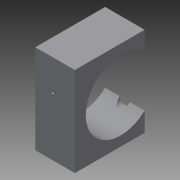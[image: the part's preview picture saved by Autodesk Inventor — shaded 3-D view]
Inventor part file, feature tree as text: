
AUTODESK INVENTOR PART (.ipt)
format: ipt  version: 2015 SP2 (Build 190223200, 223)  size: 101,888 bytes
history: native  units: mm
features: sketch x6, hole x3, extrude x1
ambient origin geometry x8: Origin, YZ Plane, XZ Plane, XY Plane, X Axis, Y Axis, Z Axis, Center Point
bodies: Solid1 (feature_tree)
feature tree (10):
  extrude  "Extrusion1"  Depth=70.0mm
  hole  "Hole1"  [1 undecoded]
  sketch  "Sketch3"  dims[d5=54.75mm d6=6.0mm d7=4.0mm d8=2.0mm d9=90.0deg d10=8.0mm d11=20.594885mm d12=8.0mm]
  sketch  "Sketch4"  dims[d13=8.0mm]
  sketch  "Sketch5"  dims[d14=8.0mm d15=6.0mm d16=4.0mm d17=2.0mm d18=90.0deg d19=8.0mm d20=20.594885mm]
  hole  "Hole2"  [1 undecoded]
  hole  "Hole3"  [1 undecoded]
  sketch  "Sketch6"  dims[d21=8.0mm d22=6.0mm d23=4.0mm d24=2.0mm d25=90.0deg d26=8.0mm d27=20.594885mm]
  sketch  "Sketch1"  dims[d0=31.0mm d1=70.0mm]
  sketch  "Sketch2"  dims[d2=54.75mm d3=0.0mm d4=54.75mm]
note: 3 required parameter values undecoded (feature->parameter linkage not recoverable at this tier; creation-order binding heuristic only, values carry confidence <= 0.55)
